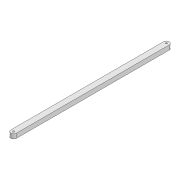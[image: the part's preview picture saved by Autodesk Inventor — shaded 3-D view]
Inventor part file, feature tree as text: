
AUTODESK INVENTOR PART (.ipt)
format: ipt  version: 2022 (Build 260153000, 153)  size: 105,984 bytes
history: native  units: mm
features: extrude x1, sketch x1
ambient origin geometry x8: Origin, YZ Plane, XZ Plane, XY Plane, X Axis, Y Axis, Z Axis, Center Point
bodies: Solid1 (feature_tree)
feature tree (2):
  extrude  "Extrusion1"  Depth=8.0mm
  sketch  "Sketch1"  dims[d0=270.69mm d1=8.0mm d2=3.0mm d3=3.0mm d4=8.0mm d5=0.0mm d10=3.0mm d11=19.5mm d12=80.0mm d13=85.0mm d14=220.0mm d15=700.0mm d16=700.0mm]
